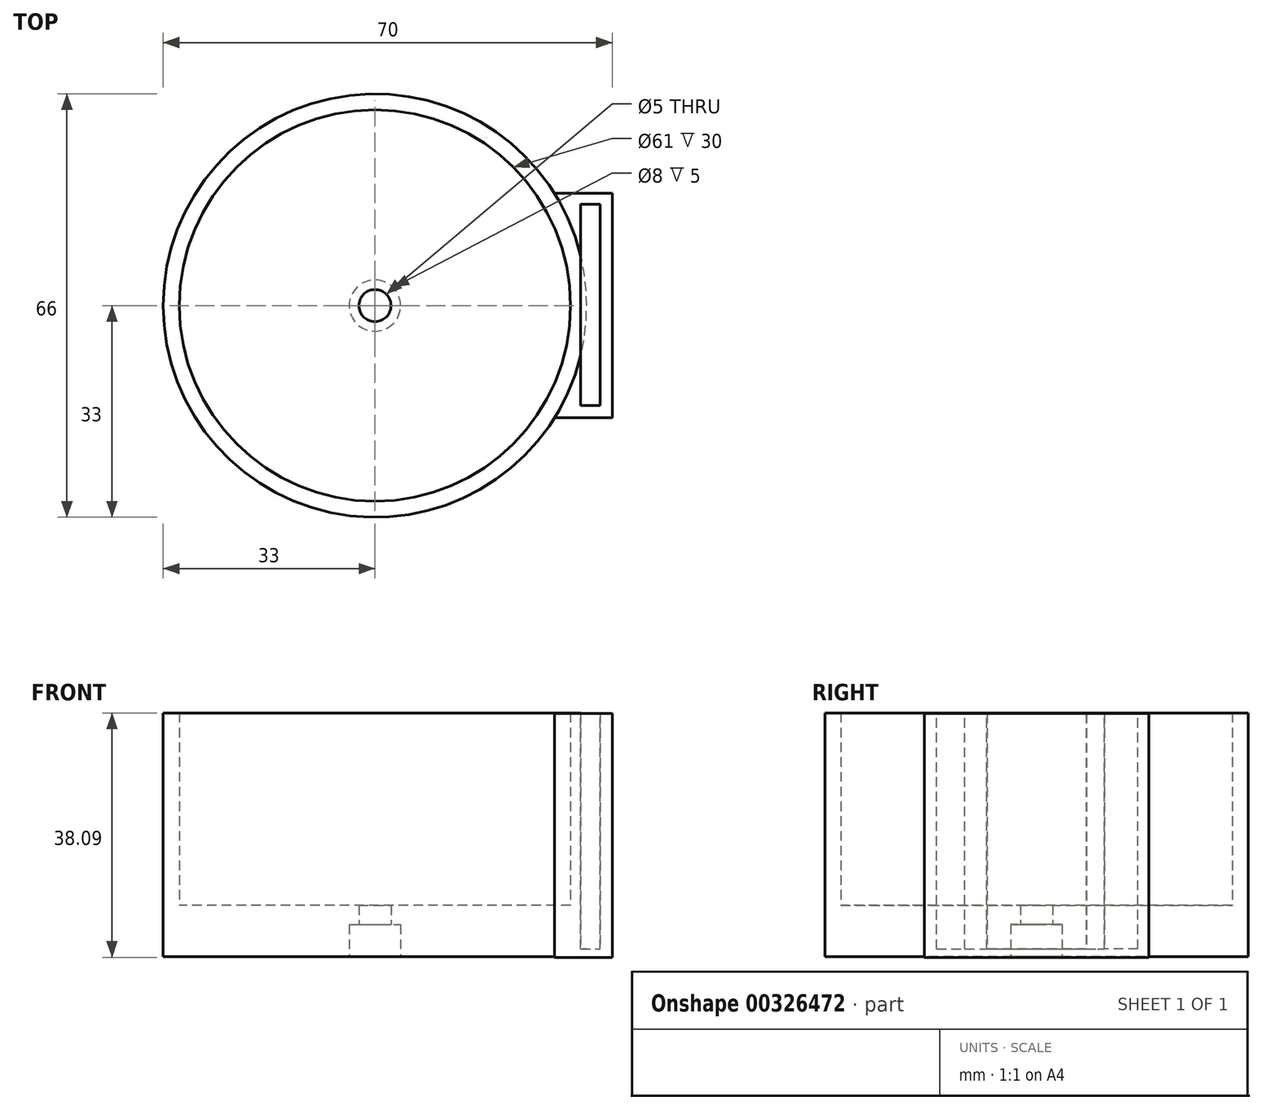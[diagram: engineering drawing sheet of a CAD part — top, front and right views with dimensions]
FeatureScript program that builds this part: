
annotation { "Feature Type Name" : "Feature", "Feature Type Description" : "" }
export const myFeature = defineFeature(function(context is Context, id is Id, definition is map)
    precondition{}
    {
        {
            var Q0;
            Q0=qCreatedBy(makeId("Top.planeOp"),FACE);
            var sketch = newSketch(context, id + "F0", { "sketchPlane" : qUnion([Q0])});
            skCircle(sketch, "E0", {"center": v(0, 0) * mm, "radius": 30.5 * mm});
            skCircle(sketch, "E1", {"center": v(0, 0) * mm, "radius": 33 * mm});
            skSolve(sketch);
        }
        {
            var Q0;
            Q0=qSketchRegion(id+"F0",true);
            extrude(context, id + "F1", {"entities" : qUnion([Q0]), "depth" : 30 * mm});
        }
        {
            var Q0;
            Q0=qCreatedBy(makeId("Right.planeOp"),FACE);
            cPlane(context, id + "F2", {"entities" : qUnion([Q0]), "cplaneType" : CPlaneType.OFFSET, "offset" : 33 * mm, "width" : 150 * mm, "height" : 150 * mm});
        }
        {
            var Q0;
            Q0=qCreatedBy(id+"F2.planeOp",FACE);
            var sketch = newSketch(context, id + "F3", { "sketchPlane" : qUnion([Q0])});
            skLineSegment(sketch, "E2.bottom", {"start": v(-17.5, 29.9) * mm, "end": v(17.5, 29.9) * mm});
            skLineSegment(sketch, "E2.top", {"start": v(-17.5, -0.1) * mm, "end": v(17.5, -0.1) * mm});
            skLineSegment(sketch, "E2.left", {"start": v(-17.5, 29.9) * mm, "end": v(-17.5, -0.1) * mm});
            skLineSegment(sketch, "E2.right", {"start": v(17.5, 29.9) * mm, "end": v(17.5, -0.1) * mm});
            skPoint(sketch, "E2.middle", {"position": v(0, 14.9) * mm});
            skSolve(sketch);
        }
        {
            var Q0;
            Q0=qSketchRegion(id+"F3",true);
            extrude(context, id + "F4", {"entities" : qUnion([Q0]), "depth" : 4 * mm});
        }
        {
            var Q0;
            Q0=makeQuery(id+"F4.opExtrude","CAP_FACE",FACE,{"disambiguationData":[OSD([sQuery(id+"F3.wireOp",EDGE,"E2.bottom"),sQuery(id+"F3.wireOp",EDGE,"E2.top"),sQuery(id+"F3.wireOp",EDGE,"E2.left"),sQuery(id+"F3.wireOp",EDGE,"E2.right")])],"isStart":true});
            extrude(context, id + "F5", {"entities" : qUnion([Q0]), "operationType" : NewBodyOperationType.ADD, "depth" : 5.5 * mm});
        }
        {
            var Q0;
            Q0=makeQuery(id+"F1.opExtrude","CAP_FACE",FACE,{"disambiguationData":[OSD([sQuery(id+"F0.wireOp",EDGE,"E0"),sQuery(id+"F0.wireOp",EDGE,"E1")])],"isStart":false});
            var sketch = newSketch(context, id + "F6", { "sketchPlane" : qUnion([Q0])});
            skCircle(sketch, "E3", {"center": v(0, 0) * mm, "radius": 30.5 * mm});
            skSolve(sketch);
        }
        {
            var Q0;
            Q0=makeQuery(id+"F6.imprint","IMPRINT",FACE,{"disambiguationData":[TD([[makeQuery(id+"F6.imprint","IMPRINT",EDGE,{"derivedFrom":sQuery(id+"F6.wireOp",EDGE,"E3")}),1.0]])]});
            extrude(context, id + "F7", {"entities" : qUnion([Q0]), "operationType" : NewBodyOperationType.REMOVE, "oppositeDirection" : true, "depth" : 40 * mm});
        }
        {
            var Q0;
            Q0=qCreatedBy(makeId("Top.planeOp"),FACE);
            var sketch = newSketch(context, id + "F8", { "sketchPlane" : qUnion([Q0])});
            skCircle(sketch, "E4", {"center": v(0, 0) * mm, "radius": 33 * mm});
            skSolve(sketch);
        }
        {
            var Q0;
            Q0=qSketchRegion(id+"F8",true);
            extrude(context, id + "F9", {"entities" : qUnion([Q0]), "operationType" : NewBodyOperationType.ADD, "oppositeDirection" : true, "depth" : 3 * mm});
        }
        {
            var Q0;
            Q0=makeQuery(id+"F9.opExtrude","CAP_FACE",FACE,{"disambiguationData":[OSD([sQuery(id+"F8.wireOp",EDGE,"E4")])],"isStart":false});
            var sketch = newSketch(context, id + "F10", { "sketchPlane" : qUnion([Q0])});
            skCircle(sketch, "E5", {"center": v(0, 0) * mm, "radius": 2.5 * mm});
            skSolve(sketch);
        }
        {
            var Q0;
            Q0=makeQuery(id+"F10.imprint","IMPRINT",FACE,{"disambiguationData":[TD([[makeQuery(id+"F10.imprint","IMPRINT",EDGE,{"derivedFrom":sQuery(id+"F10.wireOp",EDGE,"E5")}),1.0]])]});
            extrude(context, id + "F11", {"entities" : qUnion([Q0]), "operationType" : NewBodyOperationType.REMOVE, "oppositeDirection" : true, "depth" : 25 * mm});
        }
        {
            var Q0;
            Q0=makeQuery(id+"F9.opExtrude","CAP_FACE",FACE,{"disambiguationData":[OSD([sQuery(id+"F8.wireOp",EDGE,"E4")])],"isStart":false});
            extrude(context, id + "F12", {"entities" : qUnion([Q0]), "operationType" : NewBodyOperationType.ADD, "depth" : 5 * mm});
        }
        {
            var Q0;
            Q0=makeQuery(id+"F12.opExtrude","CAP_FACE",FACE,{"disambiguationData":[OSD([sQuery(id+"F8.wireOp",EDGE,"E4")])],"isStart":false});
            var sketch = newSketch(context, id + "F13", { "sketchPlane" : qUnion([Q0])});
            skCircle(sketch, "E6", {"center": v(0, 0) * mm, "radius": 4 * mm});
            skSolve(sketch);
        }
        {
            var Q0;
            Q0=makeQuery(id+"F13.imprint","IMPRINT",FACE,{"disambiguationData":[TD([[makeQuery(id+"F13.imprint","IMPRINT",EDGE,{"derivedFrom":sQuery(id+"F13.wireOp",EDGE,"E6")}),1.0]])]});
            extrude(context, id + "F14", {"entities" : qUnion([Q0]), "operationType" : NewBodyOperationType.REMOVE, "oppositeDirection" : true, "depth" : 5 * mm});
        }
        {
            var Q0;
            {var subQ0=sQuery(id+"F3.wireOp",EDGE,"E2.top");Q0=makeQuery(id+"F5.boolean.opBoolean","MERGE",FACE,{"derivedFrom":[makeQuery(id+"F4.opExtrude","SWEPT_FACE",FACE,{"disambiguationData":[OSD([subQ0])]}),makeQuery(id+"F5.opExtrude","SWEPT_FACE",FACE,{"disambiguationData":[OSD([subQ0])]})]});}
            extrude(context, id + "F15", {"entities" : qUnion([Q0]), "operationType" : NewBodyOperationType.ADD, "depth" : 8 * mm});
        }
        {
            var Q0;
            Q0=makeQuery(id+"F4.opExtrude","SWEPT_FACE",FACE,{"disambiguationData":[OSD([sQuery(id+"F3.wireOp",EDGE,"E2.bottom")])]});
            var sketch = newSketch(context, id + "F16", { "sketchPlane" : qUnion([Q0])});
            skLineSegment(sketch, "E7.bottom", {"start": v(32.07, 15.81) * mm, "end": v(35.09, 15.81) * mm});
            skLineSegment(sketch, "E7.top", {"start": v(32.07, -15.59) * mm, "end": v(35.09, -15.59) * mm});
            skLineSegment(sketch, "E7.left", {"start": v(32.07, 15.81) * mm, "end": v(32.07, -15.59) * mm});
            skLineSegment(sketch, "E7.right", {"start": v(35.09, 6.7) * mm, "end": v(35.09, -15.59) * mm});
            skLineSegment(sketch, "E8.left", {"start": v(35.09, 13.5) * mm, "end": v(35.09, -14.74) * mm});
            skLineSegment(sketch, "E9", {"start": v(35.09, 15.81) * mm, "end": v(35.09, 13.5) * mm});
            skLineSegment(sketch, "E10.left", {"start": v(35.09, 14.66) * mm, "end": v(35.09, -12.34) * mm});
            skLineSegment(sketch, "E11", {"start": v(37.05, 13.63) * mm, "end": v(37.05, -13.37) * mm});
            skLineSegment(sketch, "E12", {"start": v(37.05, 13.63) * mm, "end": v(35.09, 13.63) * mm});
            skLineSegment(sketch, "E13", {"start": v(37.05, -13.37) * mm, "end": v(35.09, -13.37) * mm});
            skSolve(sketch);
        }
        {
            var Q0;
            Q0=makeQuery(id+"F16.imprint","IMPRINT",FACE,{"disambiguationData":[TD([[makeQuery(id+"F16.imprint","IMPRINT",EDGE,{"derivedFrom":sQuery(id+"F16.wireOp",EDGE,"E7.bottom")}),-1.0]])]});
            var Q1;
            {var subQ1=sQuery(id+"F16.wireOp",EDGE,"E10.left");var subQ5=makeQuery(id+"F16.imprint","IMPRINT",VERTEX,{"derivedFrom":subQ1});Q1=makeQuery(id+"F16.imprint","IMPRINT",FACE,{"disambiguationData":[TD([[makeQuery(id+"F16.imprint","IMPRINT",EDGE,{"disambiguationData":[TD([[subQ5,1.0]])],"derivedFrom":subQ1}),1.0]])]});}
            extrude(context, id + "F17", {"entities" : qUnion([Q0, Q1]), "operationType" : NewBodyOperationType.REMOVE, "oppositeDirection" : true, "depth" : 36.7 * mm});
        }
        {
            var Q0;
            Q0=makeQuery(id+"F1.opExtrude","CAP_FACE",FACE,{"disambiguationData":[OSD([sQuery(id+"F0.wireOp",EDGE,"E0"),sQuery(id+"F0.wireOp",EDGE,"E1")])],"isStart":false});
            var sketch = newSketch(context, id + "F18", { "sketchPlane" : qUnion([Q0])});
            skLineSegment(sketch, "E14", {"start": v(32.08, 10.6) * mm, "end": v(32.08, -11.18) * mm});
            skLineSegment(sketch, "E15", {"start": v(32.08, -11.18) * mm, "end": v(35.12, -11.18) * mm});
            skLineSegment(sketch, "E16", {"start": v(35.12, -11.18) * mm, "end": v(35.12, 10.6) * mm});
            skLineSegment(sketch, "E17", {"start": v(35.12, 10.6) * mm, "end": v(32.08, 10.6) * mm});
            skSolve(sketch);
        }
        {
            var Q0;
            Q0 = qSketchRegion(id + "F18", true);
            extrude(context, id + "F19", {"entities" : qUnion([Q0]), "operationType" : NewBodyOperationType.REMOVE, "oppositeDirection" : true, "depth" : 36.8 * mm});
        }
    });
